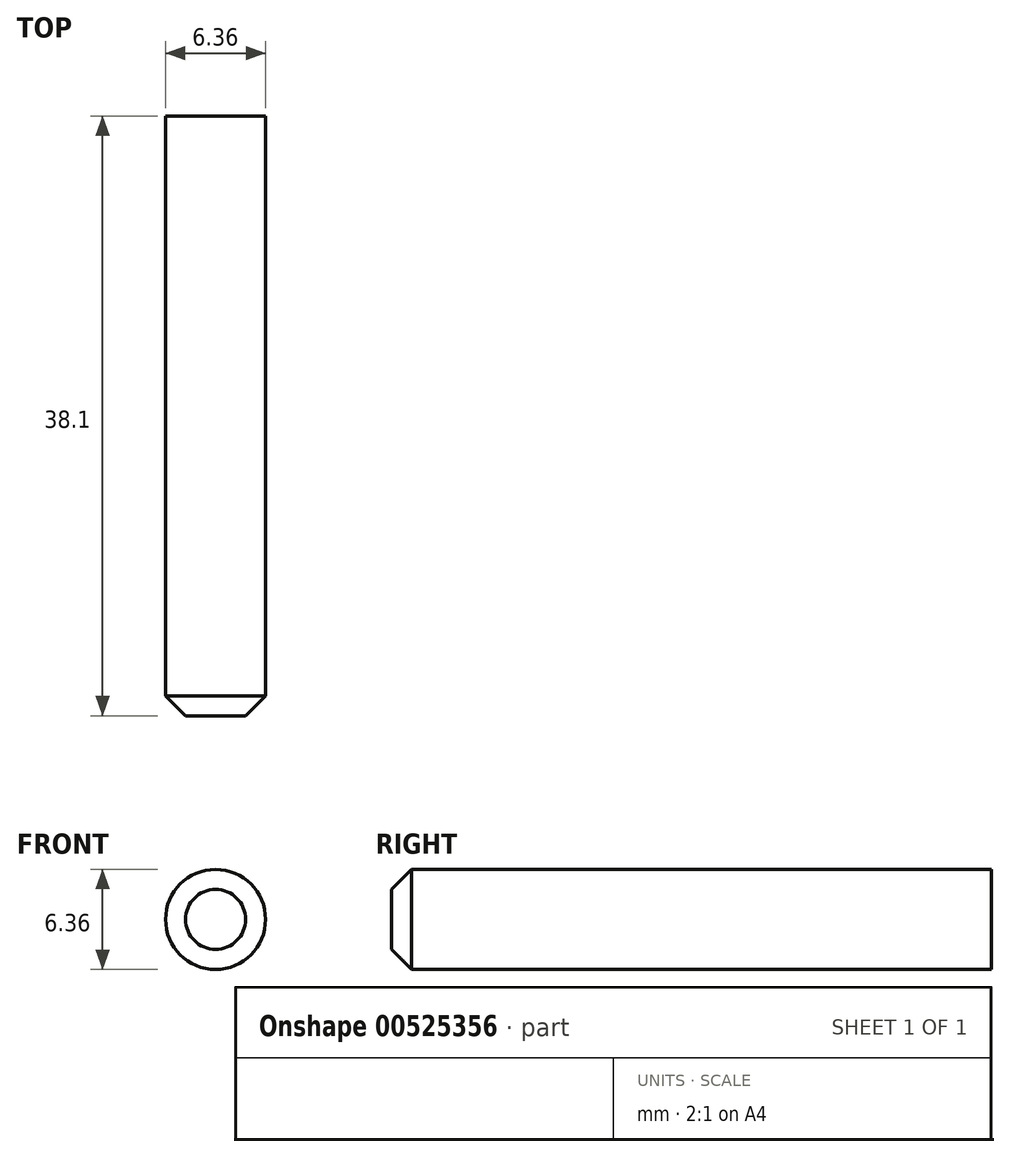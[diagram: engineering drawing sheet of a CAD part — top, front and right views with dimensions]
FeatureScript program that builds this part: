
annotation { "Feature Type Name" : "Feature", "Feature Type Description" : "" }
export const myFeature = defineFeature(function(context is Context, id is Id, definition is map)
    precondition{}
    {
        {
            var Q0;
            Q0=qCreatedBy(makeId("Front.planeOp"),FACE);
            var sketch = newSketch(context, id + "F0", { "sketchPlane" : qUnion([Q0])});
            skCircle(sketch, "E0", {"center": v(0, 0) * mm, "radius": 3.18 * mm});
            skSolve(sketch);
        }
        {
            var Q0;
            Q0 = qSketchRegion(id + "F0", true);
            extrude(context, id + "F1", {"entities" : qUnion([Q0]), "depth" : 38.1 * mm, "offsetDistance" : 25.4 * mm});
        }
        {
            var Q0;
            Q0=makeQuery(id+"F1.opExtrude","CAP_FACE",FACE,{"disambiguationData":[OSD([sQuery(id+"F0.wireOp",EDGE,"E0")])],"isStart":false});
            chamfer(context, id + "F2", {"entities" : qUnion([Q0]), "width" : 1.27 * mm, "tangentPropagation" : true});
        }
    });
